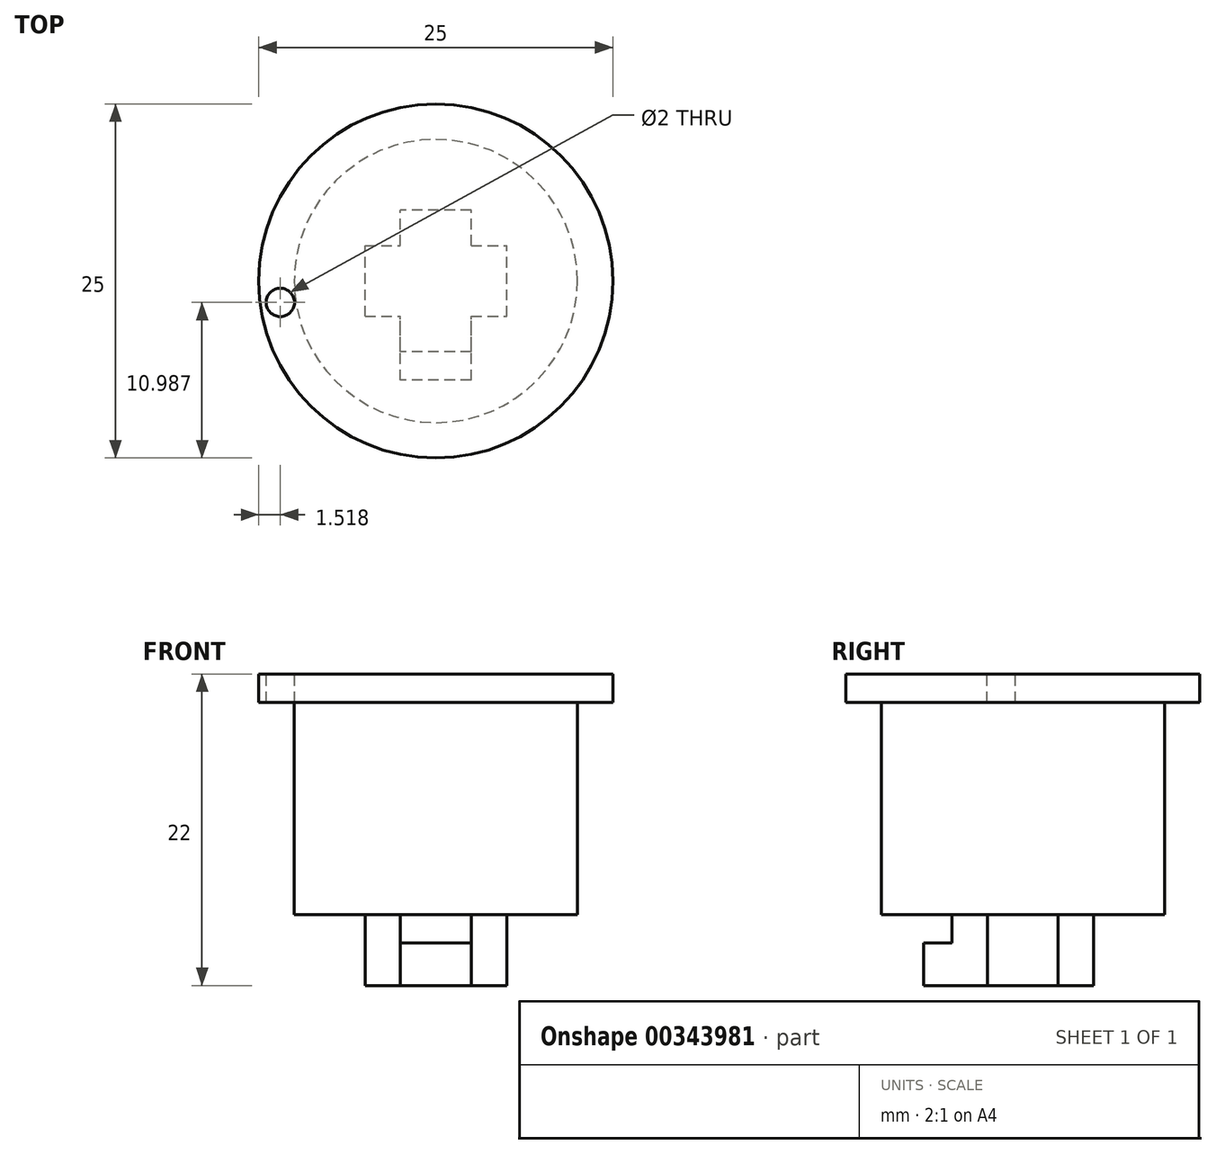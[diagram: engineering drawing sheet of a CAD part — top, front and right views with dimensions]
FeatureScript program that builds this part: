
annotation { "Feature Type Name" : "Feature", "Feature Type Description" : "" }
export const myFeature = defineFeature(function(context is Context, id is Id, definition is map)
    precondition{}
    {
        {
            var Q0;
            Q0=qCreatedBy(makeId("Top.planeOp"),FACE);
            var sketch = newSketch(context, id + "F0", { "sketchPlane" : qUnion([Q0])});
            skCircle(sketch, "E0", {"center": v(0, 0) * mm, "radius": 10 * mm});
            skSolve(sketch);
        }
        {
            var Q0;
            Q0 = qSketchRegion(id + "F0", true);
            extrude(context, id + "F1", {"entities" : qUnion([Q0]), "depth" : 15 * mm});
        }
        {
            var Q0;
            Q0=makeQuery(id+"F1.opExtrude","CAP_FACE",FACE,{"disambiguationData":[OSD([sQuery(id+"F0.wireOp",EDGE,"E0")])],"isStart":false});
            var sketch = newSketch(context, id + "F2", { "sketchPlane" : qUnion([Q0])});
            skCircle(sketch, "E1", {"center": v(0, 0) * mm, "radius": 12.5 * mm});
            skSolve(sketch);
        }
        {
            var Q0;
            Q0 = qSketchRegion(id + "F2", true);
            extrude(context, id + "F3", {"entities" : qUnion([Q0]), "operationType" : NewBodyOperationType.ADD, "depth" : 2 * mm});
        }
        {
            var Q0;
            Q0=makeQuery(id+"F1.opExtrude","CAP_FACE",FACE,{"disambiguationData":[OSD([sQuery(id+"F0.wireOp",EDGE,"E0")])],"isStart":true});
            var sketch = newSketch(context, id + "F4", { "sketchPlane" : qUnion([Q0])});
            skLineSegment(sketch, "E2.bottom", {"start": v(-5, 2.5) * mm, "end": v(5, 2.5) * mm});
            skLineSegment(sketch, "E2.top", {"start": v(-5, -2.5) * mm, "end": v(5, -2.5) * mm});
            skLineSegment(sketch, "E2.left", {"start": v(-5, 2.5) * mm, "end": v(-5, -2.5) * mm});
            skLineSegment(sketch, "E2.right", {"start": v(5, 2.5) * mm, "end": v(5, -2.5) * mm});
            skPoint(sketch, "E2.middle", {"position": v(0, 0) * mm});
            skLineSegment(sketch, "E3.bottom", {"start": v(2.5, 5) * mm, "end": v(-2.5, 5) * mm});
            skLineSegment(sketch, "E3.top", {"start": v(2.5, -5) * mm, "end": v(-2.5, -5) * mm});
            skLineSegment(sketch, "E3.left", {"start": v(2.5, 5) * mm, "end": v(2.5, -5) * mm});
            skLineSegment(sketch, "E3.right", {"start": v(-2.5, 5) * mm, "end": v(-2.5, -5) * mm});
            skSolve(sketch);
        }
        {
            var Q0;
            Q0 = qSketchRegion(id + "F4", true);
            extrude(context, id + "F5", {"entities" : qUnion([Q0]), "operationType" : NewBodyOperationType.ADD, "depth" : 5 * mm});
        }
        {
            var Q0;
            Q0=makeQuery(id+"F5.opExtrude","SWEPT_FACE",FACE,{"disambiguationData":[OSD([sQuery(id+"F4.wireOp",EDGE,"E3.bottom")])]});
            var sketch = newSketch(context, id + "F6", { "sketchPlane" : qUnion([Q0])});
            skLineSegment(sketch, "E4.bottom", {"start": v(-2.5, -5) * mm, "end": v(2.5, -5) * mm});
            skLineSegment(sketch, "E4.top", {"start": v(-2.5, -2) * mm, "end": v(2.5, -2) * mm});
            skLineSegment(sketch, "E4.left", {"start": v(-2.5, -5) * mm, "end": v(-2.5, -2) * mm});
            skLineSegment(sketch, "E4.right", {"start": v(2.5, -5) * mm, "end": v(2.5, -2) * mm});
            skSolve(sketch);
        }
        {
            var Q0;
            Q0 = qSketchRegion(id + "F6", true);
            extrude(context, id + "F7", {"entities" : qUnion([Q0]), "operationType" : NewBodyOperationType.ADD, "depth" : 2 * mm});
        }
        {
            var Q0;
            Q0=makeQuery(id+"F3.opExtrude","CAP_FACE",FACE,{"disambiguationData":[OSD([sQuery(id+"F2.wireOp",EDGE,"E1")])],"isStart":false});
            var sketch = newSketch(context, id + "F8", { "sketchPlane" : qUnion([Q0])});
            skCircle(sketch, "E5", {"center": v(-10.98, -1.51) * mm, "radius": 1 * mm});
            skSolve(sketch);
        }
        {
            var Q0;
            Q0 = qSketchRegion(id + "F8", true);
            extrude(context, id + "F9", {"entities" : qUnion([Q0]), "operationType" : NewBodyOperationType.REMOVE, "oppositeDirection" : true, "depth" : 3 * mm});
        }
    });
